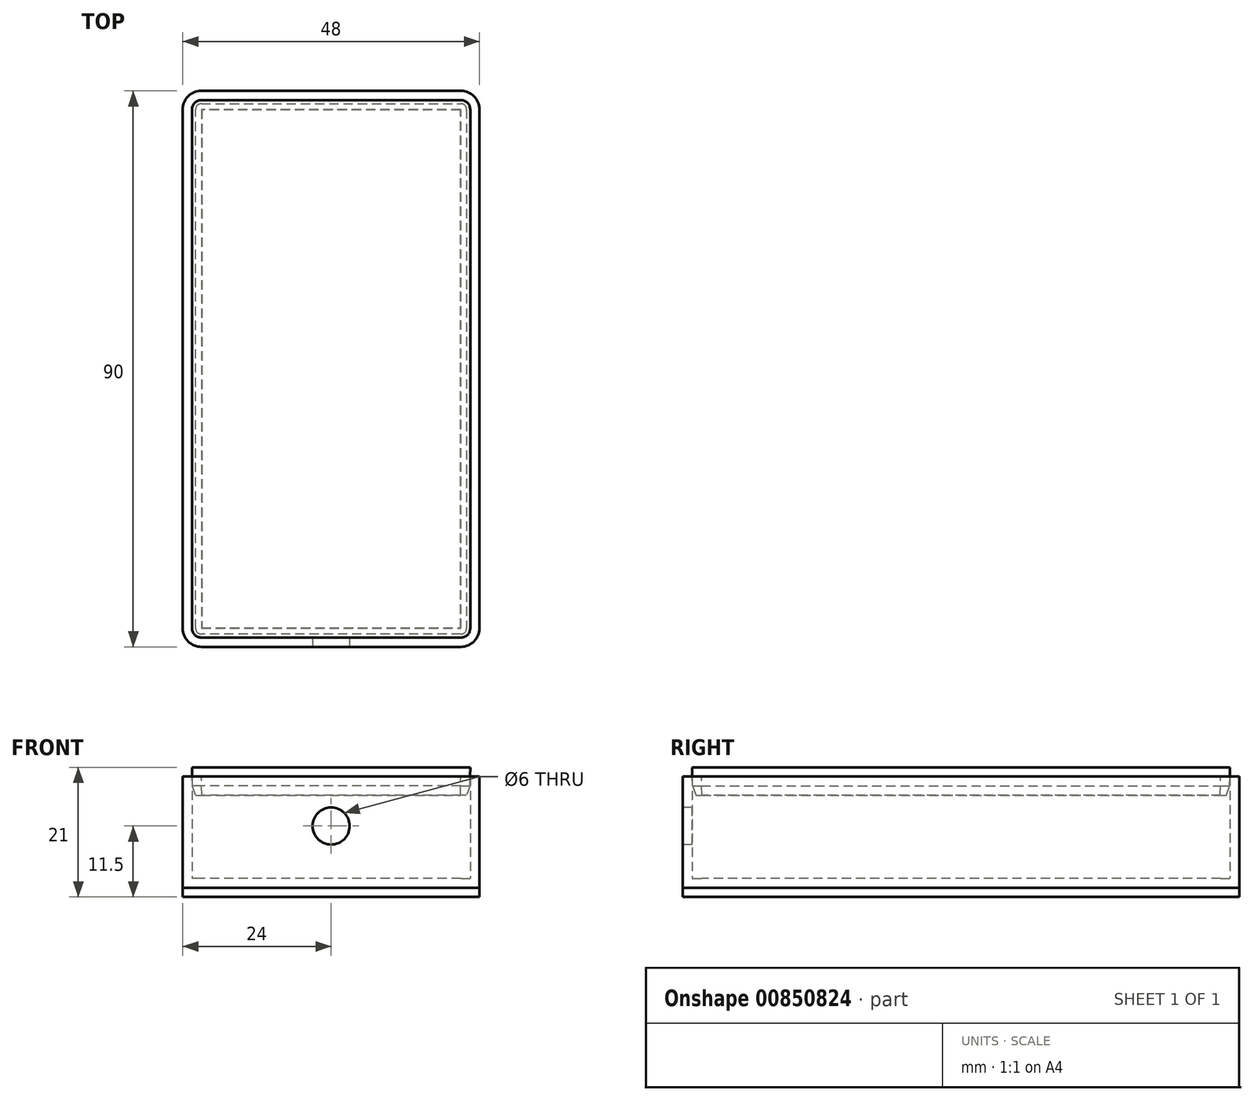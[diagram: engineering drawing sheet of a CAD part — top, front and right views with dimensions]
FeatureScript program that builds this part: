
annotation { "Feature Type Name" : "Feature", "Feature Type Description" : "" }
export const myFeature = defineFeature(function(context is Context, id is Id, definition is map)
    precondition{}
    {
        {
            assignVariable(context, id + "F0", {"name" : "alto", "anyValue" : 18});
        }
        {
            assignVariable(context, id + "F1", {"name" : "espesor", "anyValue" : 1.5});
        }
        {
            var Q0;
            Q0=qCreatedBy(makeId("Top.planeOp"),FACE);
            var sketch = newSketch(context, id + "F2", { "sketchPlane" : qUnion([Q0])});
            skLineSegment(sketch, "E0.bottom", {"start": v(21, 45) * mm, "end": v(-21, 45) * mm});
            skLineSegment(sketch, "E0.top", {"start": v(21, -45) * mm, "end": v(-21, -45) * mm});
            skLineSegment(sketch, "E0.left", {"start": v(24, 42) * mm, "end": v(24, -42) * mm});
            skLineSegment(sketch, "E0.right", {"start": v(-24, 42) * mm, "end": v(-24, -42) * mm});
            skPoint(sketch, "E0.middle", {"position": v(0, 0) * mm});
            skPoint(sketch, "E1.visualSharp", {"position": v(-24, -45) * mm});
            skArc(sketch, "E1.filletArc", {"start": v(-24, -42) * mm, "mid": v(-23.12, -44.12) * mm, "end": v(-21, -45) * mm});
            skPoint(sketch, "E2.visualSharp", {"position": v(24, -45) * mm});
            skArc(sketch, "E2.filletArc", {"start": v(21, -45) * mm, "mid": v(23.12, -44.12) * mm, "end": v(24, -42) * mm});
            skPoint(sketch, "E3.visualSharp", {"position": v(24, 45) * mm});
            skArc(sketch, "E3.filletArc", {"start": v(24, 42) * mm, "mid": v(23.12, 44.12) * mm, "end": v(21, 45) * mm});
            skPoint(sketch, "E4.visualSharp", {"position": v(-24, 45) * mm});
            skArc(sketch, "E4.filletArc", {"start": v(-21, 45) * mm, "mid": v(-23.12, 44.12) * mm, "end": v(-24, 42) * mm});
            skSolve(sketch);
        }
        {
            var Q0;
            Q0=makeQuery(id+"F2.imprint","IMPRINT",FACE,{"disambiguationData":[TD([[makeQuery(id+"F2.imprint","IMPRINT",EDGE,{"derivedFrom":sQuery(id+"F2.wireOp",EDGE,"E0.bottom")}),1.0]])]});
            extrude(context, id + "F3", {"entities" : qUnion([Q0]), "depth" : (getVariable(context, 'alto')) * mm, "offsetDistance" : 25 * mm});
        }
        {
            var Q0;
            Q0=makeQuery(id+"F3.opExtrude","CAP_FACE",FACE,{"disambiguationData":[OSD([sQuery(id+"F2.wireOp",EDGE,"E0.bottom"),sQuery(id+"F2.wireOp",EDGE,"E0.top"),sQuery(id+"F2.wireOp",EDGE,"E0.left"),sQuery(id+"F2.wireOp",EDGE,"E0.right")])],"isStart":false});
            shell(context, id + "F4", {"entities" : qUnion([Q0]), "thickness" : (getVariable(context, 'espesor')) * mm});
        }
        {
            var Q0;
            Q0=makeQuery(id+"F3.opExtrude","SWEPT_FACE",FACE,{"disambiguationData":[OSD([sQuery(id+"F2.wireOp",EDGE,"E0.top")])]});
            var sketch = newSketch(context, id + "F5", { "sketchPlane" : qUnion([Q0])});
            skLineSegment(sketch, "E5.0.0", {"start": v(-21, 0) * mm, "end": v(21, 0) * mm});
            skLineSegment(sketch, "E5.0.1", {"start": v(21, 0) * mm, "end": v(21, 18) * mm});
            skLineSegment(sketch, "E5.0.2", {"start": v(21, 18) * mm, "end": v(-21, 18) * mm});
            skLineSegment(sketch, "E5.0.3", {"start": v(-21, 18) * mm, "end": v(-21, 0) * mm});
            skCircle(sketch, "E6", {"center": v(0, 10) * mm, "radius": 3 * mm});
            skSolve(sketch);
        }
        {
            var Q0;
            Q0=makeQuery(id+"F5.imprint","IMPRINT",FACE,{"disambiguationData":[TD([[makeQuery(id+"F5.imprint","IMPRINT",EDGE,{"derivedFrom":sQuery(id+"F5.wireOp",EDGE,"E6")}),1.0]])]});
            extrude(context, id + "F6", {"entities" : qUnion([Q0]), "operationType" : NewBodyOperationType.REMOVE, "oppositeDirection" : true, "depth" : 25 * mm, "offsetDistance" : 25 * mm});
        }
        {
            var Q0;
            Q0=makeQuery(id+"F2.imprint","IMPRINT",FACE,{"disambiguationData":[TD([[makeQuery(id+"F2.imprint","IMPRINT",EDGE,{"derivedFrom":sQuery(id+"F2.wireOp",EDGE,"E0.bottom")}),1.0]])]});
            var Q1;
            Q1=qCreatedBy(makeId("Top.planeOp"),FACE);
            var Q2;
            Q2=makeQuery(id+"F2.imprint","IMPRINT",FACE,{"disambiguationData":[TD([[makeQuery(id+"F2.imprint","IMPRINT",EDGE,{"derivedFrom":sQuery(id+"F2.wireOp",EDGE,"E0.bottom")}),1.0]])]});
            var Q3;
            Q3=makeQuery(id+"F2.imprint","IMPRINT",FACE,{"disambiguationData":[TD([[makeQuery(id+"F2.imprint","IMPRINT",EDGE,{"derivedFrom":sQuery(id+"F2.wireOp",EDGE,"E0.bottom")}),1.0]])]});
            var Q4;
            Q4=qCreatedBy(makeId("Top.planeOp"),FACE);
            var sketch = newSketch(context, id + "F7", { "sketchPlane" : qUnion([Q0, Q1, Q2, Q3, Q4])});
            skArc(sketch, "E7.0", {"start": v(-22.5, -42) * mm, "mid": v(-22.06, -43.06) * mm, "end": v(-21, -43.5) * mm});
            skArc(sketch, "E8.0", {"start": v(21, -43.5) * mm, "mid": v(22.06, -43.06) * mm, "end": v(22.5, -42) * mm});
            skArc(sketch, "E9.0", {"start": v(-21, 43.5) * mm, "mid": v(-22.06, 43.06) * mm, "end": v(-22.5, 42) * mm});
            skArc(sketch, "E10.0", {"start": v(22.5, 42) * mm, "mid": v(22.06, 43.06) * mm, "end": v(21, 43.5) * mm});
            skLineSegment(sketch, "E11", {"start": v(-21, -43.5) * mm, "end": v(21, -43.5) * mm});
            skLineSegment(sketch, "E12", {"start": v(22.5, -42) * mm, "end": v(22.5, 42) * mm});
            skLineSegment(sketch, "E13", {"start": v(21, 43.5) * mm, "end": v(-21, 43.5) * mm});
            skLineSegment(sketch, "E14", {"start": v(-22.5, 42) * mm, "end": v(-22.5, -42) * mm});
            skSolve(sketch);
        }
        {
            var Q0;
            Q0=makeQuery(id+"F7.imprint","IMPRINT",FACE,{"disambiguationData":[TD([[makeQuery(id+"F7.imprint","IMPRINT",EDGE,{"derivedFrom":makeQuery(id+"F2.imprint","IMPRINT",EDGE,{"derivedFrom":sQuery(id+"F2.wireOp",EDGE,"E0.bottom")})}),1.0]])]});
            var Q1;
            Q1=makeQuery(id+"F7.imprint","IMPRINT",FACE,{"disambiguationData":[TD([[makeQuery(id+"F7.imprint","IMPRINT",EDGE,{"derivedFrom":sQuery(id+"F7.wireOp",EDGE,"67830d29-e5c7-46e2-8667-b93d965edc65.0")}),-1.0]])]});
            var Q2;
            Q2=makeQuery(id+"F7.imprint","IMPRINT",FACE,{"disambiguationData":[TD([[makeQuery(id+"F7.imprint","IMPRINT",EDGE,{"derivedFrom":sQuery(id+"F7.wireOp",EDGE,"E7.0")}),1.0]])]});
            extrude(context, id + "F8", {"entities" : qUnion([Q0, Q1, Q2]), "oppositeDirection" : true, "depth" : (getVariable(context, 'espesor')) * mm, "offsetDistance" : 25 * mm});
        }
        {
            var Q0;
            Q0=makeQuery(id+"F7.imprint","IMPRINT",FACE,{"disambiguationData":[TD([[makeQuery(id+"F7.imprint","IMPRINT",EDGE,{"derivedFrom":sQuery(id+"F7.wireOp",EDGE,"67830d29-e5c7-46e2-8667-b93d965edc65.0")}),-1.0]])]});
            var Q1;
            Q1=makeQuery(id+"F7.imprint","IMPRINT",FACE,{"disambiguationData":[TD([[makeQuery(id+"F7.imprint","IMPRINT",EDGE,{"derivedFrom":sQuery(id+"F7.wireOp",EDGE,"E7.0")}),1.0]])]});
            var Q2;
            Q2=makeQuery(id+"F7.imprint","IMPRINT",FACE,{"disambiguationData":[TD([[makeQuery(id+"F7.imprint","IMPRINT",EDGE,{"derivedFrom":sQuery(id+"F7.wireOp",EDGE,"E7.0")}),1.0]])]});
            extrude(context, id + "F9", {"entities" : qUnion([Q0, Q1, Q2]), "oppositeDirection" : true, "depth" : (getVariable(context, 'espesor') * 3) * mm, "offsetDistance" : 25 * mm, "hasDraft" : true, "draftAngle" : 1 * degree, "draftPullDirection" : true});
        }
        {
            var Q0;
            Q0=makeQuery(id+"F9.opExtrude","CAP_FACE",FACE,{"disambiguationData":[OSD([sQuery(id+"F7.wireOp",EDGE,"E7.0"),sQuery(id+"F7.wireOp",EDGE,"E8.0"),sQuery(id+"F7.wireOp",EDGE,"E9.0"),sQuery(id+"F7.wireOp",EDGE,"E10.0"),sQuery(id+"F7.wireOp",EDGE,"E11"),sQuery(id+"F7.wireOp",EDGE,"E12"),sQuery(id+"F7.wireOp",EDGE,"E13"),sQuery(id+"F7.wireOp",EDGE,"E14")])],"isStart":false});
            shell(context, id + "F10", {"entities" : qUnion([Q0]), "thickness" : (getVariable(context, 'espesor')) * mm});
        }
        {
            var Q0;
            Q0=makeQuery(id+"F9.opExtrude","SWEPT_BODY",BODY,{"disambiguationData":[OSD([sQuery(id+"F7.wireOp",EDGE,"E7.0"),sQuery(id+"F7.wireOp",EDGE,"E8.0"),sQuery(id+"F7.wireOp",EDGE,"E9.0"),sQuery(id+"F7.wireOp",EDGE,"E10.0"),sQuery(id+"F7.wireOp",EDGE,"E11"),sQuery(id+"F7.wireOp",EDGE,"E12"),sQuery(id+"F7.wireOp",EDGE,"E13"),sQuery(id+"F7.wireOp",EDGE,"E14")])]});
            transform(context, id + "F11", {"entities" : qUnion([Q0]), "transformType" : TransformType.TRANSLATION_3D, "dx" : 0 * mm, "dy" : 0 * mm, "dz" : (getVariable(context, 'alto') + getVariable(context, 'espesor')) * mm, "makeCopy" : false});
        }
        {
            var Q0;
            Q0=makeQuery(id+"F9.opExtrude","CAP_EDGE",EDGE,{"disambiguationData":[OSD([sQuery(id+"F7.wireOp",EDGE,"E14")])],"isStart":false});
            chamfer(context, id + "F12", {"entities" : qUnion([Q0]), "chamferType" : ChamferType.TWO_OFFSETS, "width1" : (getVariable(context, 'espesor') / 1) * mm, "oppositeDirection" : false, "width2" : (getVariable(context, 'espesor') / 3) * mm, "tangentPropagation" : true});
        }
    });
